# Revit family: Electrical-Lutron-QS_J-Box_Power_Supply
name_source: partatom
category: Lighting Devices
revit_build: Autodesk Revit 2017 (Build: 20160225_1515(x64)
units: mm (PartAtom-declared; Revit-internal decimal feet)

## family parameters
Cut with Voids When Loaded = No
Host = Face
Maintain Annotation Orientation = Yes
OmniClass Number = 23.85.80.11.27
OmniClass Title = Lighting Controls
Part Type = Switch
Room Calculation Point = No
Round Connector Dimension = Use Diameter
Shared = No

## types (1)
- QSPS-J-1-50
    Apparent Load = 0 VA
    Assembly Code = D5020120
    Cost = 0 $
    Default Elevation = 4' - 0"
    Description = QS J-Box Power Supply
    Environment = Ambient operating temperature 32 ˚F to 104 ˚F (0 ˚C to 40 ˚C), Maximum 90% non-condensing relative humidity, Indoor use only, IP20 Rating.
    Finish = Plastic - Lutron - White - Matte
    Frequency = 50 Hz
    Input Voltage = 120 V
    Instruction Sheet Link = http://www.lutron.com
    Manufacturer = Lutron Electronics Co., Inc
    Manufacturer Fax Number = 610-282-1243
    Model = QSPS-J-1-50
    Overall Depth = 4 3/32"
    Overall Height = 1 13/32"
    Overall Width = 4 5/16"
    Performance URL = http://www.lutron.com
    Product Documentation Link = http://www.lutron.com
    Product Name = QS J-Box Power Supply
    Product Page URL = http://www.lutron.com
    Series = SivoiaQS
    URL = http://www.lutron.com
    Version = 2017 - v1.0a
    Video Link = https://www.youtube.com
    Voltage = 24 V
    Voltage Comment = 24V
    Warranty URL = http://www.lutron.com

## geometry (parser evidence)
native form markers: Sweep x3
no freeform markers — native parametric forms only
